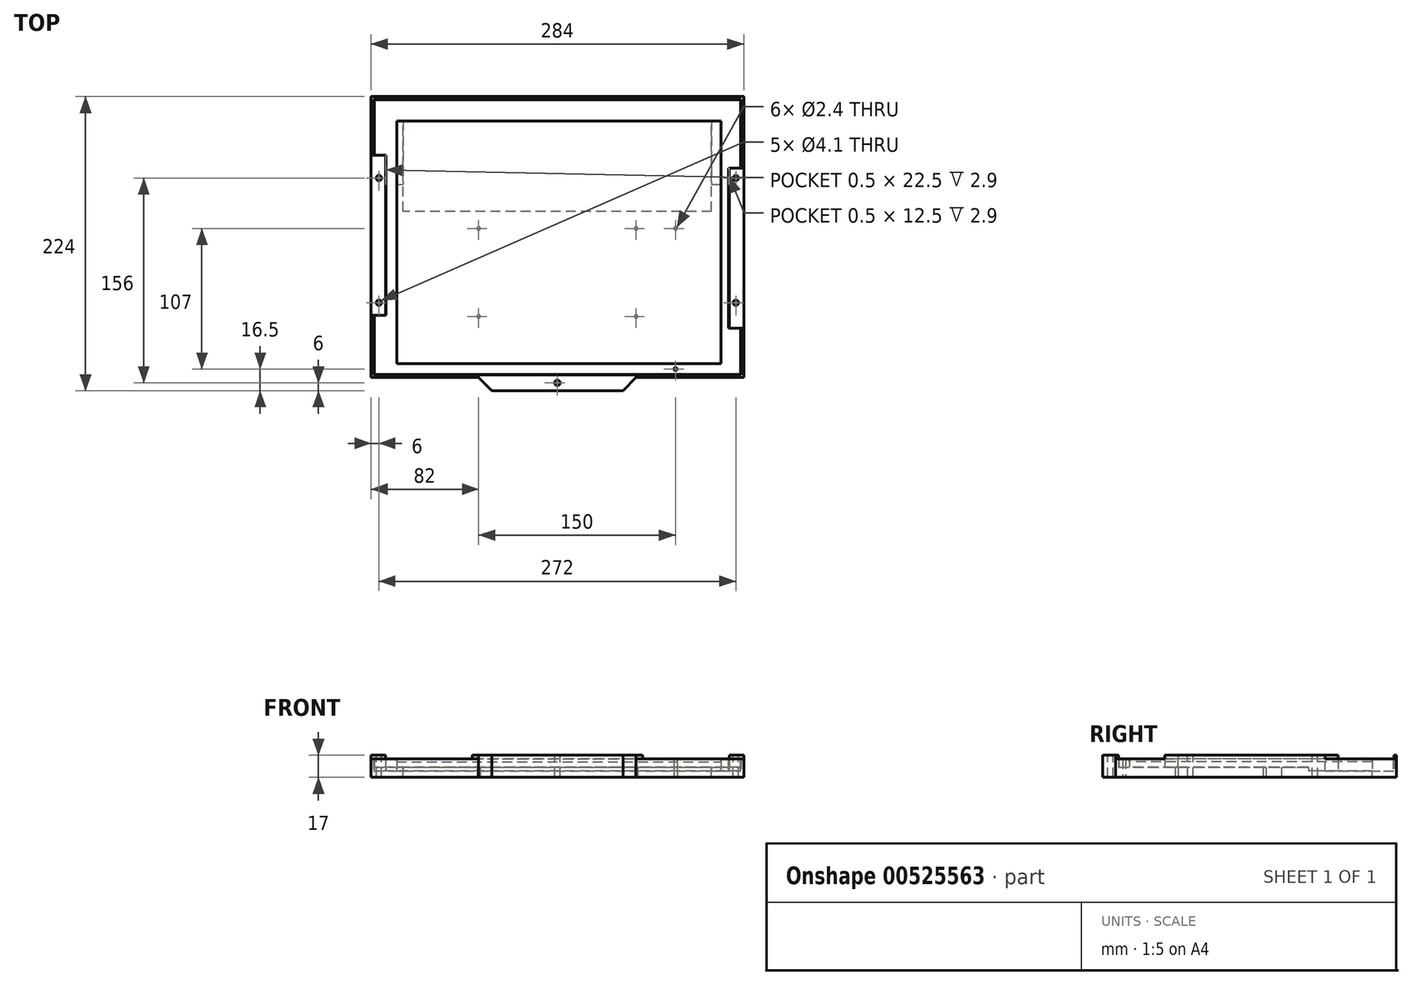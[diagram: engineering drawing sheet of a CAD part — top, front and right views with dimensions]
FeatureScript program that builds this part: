
annotation { "Feature Type Name" : "Feature", "Feature Type Description" : "" }
export const myFeature = defineFeature(function(context is Context, id is Id, definition is map)
    precondition{}
    {
        {
            var Q0;
            Q0=qCreatedBy(makeId("Top.planeOp"),FACE);
            var sketch = newSketch(context, id + "F0", { "sketchPlane" : qUnion([Q0])});
            skLineSegment(sketch, "E0.bottom", {"start": v(139.5, -104.5) * mm, "end": v(-139.5, -104.5) * mm});
            skLineSegment(sketch, "E0.top", {"start": v(139.5, 104.5) * mm, "end": v(-139.5, 104.5) * mm});
            skLineSegment(sketch, "E0.left", {"start": v(139.5, -104.5) * mm, "end": v(139.5, 104.5) * mm});
            skLineSegment(sketch, "E0.right", {"start": v(-139.5, -104.5) * mm, "end": v(-139.5, 104.5) * mm});
            skPoint(sketch, "E0.middle", {"position": v(0, 0) * mm});
            skLineSegment(sketch, "E1.bottom", {"start": v(-122.5, 88.5) * mm, "end": v(124.5, 88.5) * mm});
            skLineSegment(sketch, "E1.top", {"start": v(-122.5, -96.5) * mm, "end": v(124.5, -96.5) * mm});
            skLineSegment(sketch, "E1.left", {"start": v(-122.5, 88.5) * mm, "end": v(-122.5, -96.5) * mm});
            skLineSegment(sketch, "E1.right", {"start": v(124.5, 88.5) * mm, "end": v(124.5, -96.5) * mm});
            skSolve(sketch);
        }
        {
            var Q0;
            Q0 = qSketchRegion(id + "F0", true);
            extrude(context, id + "F1", {"entities" : qUnion([Q0]), "depth" : 9 * mm, "offsetDistance" : 25 * mm});
        }
        {
            var Q0;
            Q0=makeQuery(id+"F1.opExtrude","CAP_FACE",FACE,{"disambiguationData":[OSD([sQuery(id+"F0.wireOp",EDGE,"E0.bottom"),sQuery(id+"F0.wireOp",EDGE,"E0.top"),sQuery(id+"F0.wireOp",EDGE,"E0.left"),sQuery(id+"F0.wireOp",EDGE,"E0.right"),sQuery(id+"F0.wireOp",EDGE,"E1.bottom"),sQuery(id+"F0.wireOp",EDGE,"E1.top"),sQuery(id+"F0.wireOp",EDGE,"E1.left"),sQuery(id+"F0.wireOp",EDGE,"E1.right")])],"isStart":false});
            var sketch = newSketch(context, id + "F2", { "sketchPlane" : qUnion([Q0])});
            skLineSegment(sketch, "E2.bottom", {"start": v(-139.5, 62.5) * mm, "end": v(-130.5, 62.5) * mm});
            skLineSegment(sketch, "E2.top", {"start": v(-139.5, -59.5) * mm, "end": v(-130.5, -59.5) * mm});
            skLineSegment(sketch, "E2.left", {"start": v(-139.5, 62.5) * mm, "end": v(-139.5, -59.5) * mm});
            skLineSegment(sketch, "E2.right", {"start": v(-130.5, 62.5) * mm, "end": v(-130.5, -59.5) * mm});
            skLineSegment(sketch, "E3.bottom", {"start": v(130.5, 52.5) * mm, "end": v(139.5, 52.5) * mm});
            skLineSegment(sketch, "E3.top", {"start": v(130.5, -69.5) * mm, "end": v(139.5, -69.5) * mm});
            skLineSegment(sketch, "E3.left", {"start": v(130.5, 52.5) * mm, "end": v(130.5, -69.5) * mm});
            skLineSegment(sketch, "E3.right", {"start": v(139.5, 52.5) * mm, "end": v(139.5, -69.5) * mm});
            skSolve(sketch);
        }
        {
            var Q0;
            Q0 = qSketchRegion(id + "F2", true);
            extrude(context, id + "F3", {"entities" : qUnion([Q0]), "operationType" : NewBodyOperationType.REMOVE, "oppositeDirection" : true, "depth" : 25 * mm, "offsetDistance" : 25 * mm});
        }
        {
            var Q0;
            Q0=qCreatedBy(makeId("Top.planeOp"),FACE);
            cPlane(context, id + "F4", {"entities" : qUnion([Q0]), "cplaneType" : CPlaneType.OFFSET, "offset" : 5 * mm, "oppositeDirection" : true, "width" : 150 * mm, "height" : 150 * mm});
        }
        {
            var Q0;
            Q0=qCreatedBy(id+"F4.planeOp",FACE);
            var sketch = newSketch(context, id + "F5", { "sketchPlane" : qUnion([Q0])});
            skLineSegment(sketch, "E4.bottom", {"start": v(-142, 107) * mm, "end": v(142, 107) * mm});
            skLineSegment(sketch, "E4.top", {"start": v(-142, -107) * mm, "end": v(142, -107) * mm});
            skLineSegment(sketch, "E4.left", {"start": v(-142, 107) * mm, "end": v(-142, -107) * mm});
            skLineSegment(sketch, "E4.right", {"start": v(142, 107) * mm, "end": v(142, -107) * mm});
            skLineSegment(sketch, "E5", {"start": v(-140, 105) * mm, "end": v(140, 105) * mm});
            skLineSegment(sketch, "E6", {"start": v(140, 105) * mm, "end": v(140, 52.5) * mm});
            skLineSegment(sketch, "E7", {"start": v(140, 52.5) * mm, "end": v(131, 52.5) * mm});
            skLineSegment(sketch, "E8", {"start": v(131, 52.5) * mm, "end": v(131, -69.5) * mm});
            skLineSegment(sketch, "E9", {"start": v(131, -69.5) * mm, "end": v(140, -69.5) * mm});
            skLineSegment(sketch, "E10", {"start": v(140, -69.5) * mm, "end": v(140, -105) * mm});
            skLineSegment(sketch, "E11", {"start": v(140, -105) * mm, "end": v(-140, -105) * mm});
            skLineSegment(sketch, "E12", {"start": v(-140, -105) * mm, "end": v(-140, -59.5) * mm});
            skLineSegment(sketch, "E13", {"start": v(-140, -59.5) * mm, "end": v(-131, -59.5) * mm});
            skLineSegment(sketch, "E14", {"start": v(-131, -59.5) * mm, "end": v(-131, 62.5) * mm});
            skLineSegment(sketch, "E15", {"start": v(-131, 62.5) * mm, "end": v(-140, 62.5) * mm});
            skLineSegment(sketch, "E16", {"start": v(-140, 62.5) * mm, "end": v(-140, 105) * mm});
            skLineSegment(sketch, "E17", {"start": v(-50, -117) * mm, "end": v(50, -117) * mm});
            skLineSegment(sketch, "E18", {"start": v(50, -117) * mm, "end": v(60, -107) * mm});
            skLineSegment(sketch, "E19", {"start": v(-50, -117) * mm, "end": v(-60, -107) * mm});
            skSolve(sketch);
        }
        {
            var Q0;
            Q0 = qSketchRegion(id + "F5", true);
            extrude(context, id + "F6", {"entities" : qUnion([Q0]), "depth" : 14 * mm, "offsetDistance" : 25 * mm});
        }
        {
            var Q0;
            Q0=makeQuery(id+"F6.opExtrude","CAP_FACE",FACE,{"disambiguationData":[OSD([sQuery(id+"F5.wireOp",EDGE,"E4.bottom"),sQuery(id+"F5.wireOp",EDGE,"E4.top"),sQuery(id+"F5.wireOp",EDGE,"E4.left"),sQuery(id+"F5.wireOp",EDGE,"E4.right"),sQuery(id+"F5.wireOp",EDGE,"E5"),sQuery(id+"F5.wireOp",EDGE,"E6"),sQuery(id+"F5.wireOp",EDGE,"E7"),sQuery(id+"F5.wireOp",EDGE,"E8"),sQuery(id+"F5.wireOp",EDGE,"E9"),sQuery(id+"F5.wireOp",EDGE,"E10"),sQuery(id+"F5.wireOp",EDGE,"E11"),sQuery(id+"F5.wireOp",EDGE,"E12"),sQuery(id+"F5.wireOp",EDGE,"E13"),sQuery(id+"F5.wireOp",EDGE,"E14"),sQuery(id+"F5.wireOp",EDGE,"E15"),sQuery(id+"F5.wireOp",EDGE,"E16")])],"isStart":true});
            var sketch = newSketch(context, id + "F7", { "sketchPlane" : qUnion([Q0])});
            skLineSegment(sketch, "E20.bottom", {"start": v(140, 105) * mm, "end": v(-140, 105) * mm});
            skLineSegment(sketch, "E20.top", {"start": v(140, -105) * mm, "end": v(-140, -105) * mm});
            skLineSegment(sketch, "E20.left", {"start": v(140, 105) * mm, "end": v(140, -105) * mm});
            skLineSegment(sketch, "E20.right", {"start": v(-140, 105) * mm, "end": v(-140, -105) * mm});
            skSolve(sketch);
        }
        {
            var Q0;
            Q0 = qSketchRegion(id + "F7", true);
            extrude(context, id + "F8", {"entities" : qUnion([Q0]), "operationType" : NewBodyOperationType.ADD, "oppositeDirection" : true, "depth" : 5 * mm, "offsetDistance" : 25 * mm});
        }
        {
            var Q0;
            Q0=makeQuery(id+"F8.opExtrude","CAP_FACE",FACE,{"disambiguationData":[OSD([sQuery(id+"F7.wireOp",EDGE,"E20.bottom"),sQuery(id+"F7.wireOp",EDGE,"E20.top"),sQuery(id+"F7.wireOp",EDGE,"E20.left"),sQuery(id+"F7.wireOp",EDGE,"E20.right")])],"isStart":false});
            var sketch = newSketch(context, id + "F9", { "sketchPlane" : qUnion([Q0])});
            skPoint(sketch, "E21.oppositeSnap0", {"position": v(140, -87.25) * mm});
            skLineSegment(sketch, "E21.bottom", {"start": v(-140, -105) * mm, "end": v(140, -105) * mm});
            skLineSegment(sketch, "E21.top", {"start": v(-140, 40) * mm, "end": v(140, 40) * mm});
            skLineSegment(sketch, "E21.left", {"start": v(-140, -105) * mm, "end": v(-140, 40) * mm});
            skLineSegment(sketch, "E21.right", {"start": v(140, -105) * mm, "end": v(140, 40) * mm});
            skSolve(sketch);
        }
        {
            var Q0;
            Q0 = qSketchRegion(id + "F9", true);
            extrude(context, id + "F10", {"entities" : qUnion([Q0]), "operationType" : NewBodyOperationType.ADD, "depth" : 2.9 * mm, "offsetDistance" : 25 * mm});
        }
        {
            var Q0;
            Q0=makeQuery(id+"F10.opExtrude","CAP_FACE",FACE,{"disambiguationData":[OSD([sQuery(id+"F9.wireOp",EDGE,"E21.bottom"),sQuery(id+"F9.wireOp",EDGE,"E21.top"),sQuery(id+"F9.wireOp",EDGE,"E21.left"),sQuery(id+"F9.wireOp",EDGE,"E21.right")])],"isStart":false});
            var sketch = newSketch(context, id + "F11", { "sketchPlane" : qUnion([Q0])});
            skLineSegment(sketch, "E22.bottom", {"start": v(117.5, 19.5) * mm, "end": v(-117.5, 19.5) * mm});
            skLineSegment(sketch, "E22.top", {"start": v(117.5, 88.5) * mm, "end": v(-117.5, 88.5) * mm});
            skLineSegment(sketch, "E22.left", {"start": v(117.5, 19.5) * mm, "end": v(117.5, 88.5) * mm});
            skLineSegment(sketch, "E22.right", {"start": v(-117.5, 19.5) * mm, "end": v(-117.5, 88.5) * mm});
            skPoint(sketch, "E22.middle", {"position": v(0, 54) * mm});
            skPoint(sketch, "E23", {"position": v(0, 40) * mm});
            skSolve(sketch);
        }
        {
            var Q0;
            Q0 = qSketchRegion(id + "F11", true);
            extrude(context, id + "F12", {"entities" : qUnion([Q0]), "operationType" : NewBodyOperationType.REMOVE, "oppositeDirection" : true, "depth" : 25 * mm, "offsetDistance" : 25 * mm});
        }
        {
            var Q0;
            Q0=makeQuery(id+"F8.boolean.opBoolean","MERGE",FACE,{"derivedFrom":[makeQuery(id+"F6.opExtrude","CAP_FACE",FACE,{"disambiguationData":[OSD([sQuery(id+"F5.wireOp",EDGE,"E4.bottom"),sQuery(id+"F5.wireOp",EDGE,"E4.top"),sQuery(id+"F5.wireOp",EDGE,"E4.left"),sQuery(id+"F5.wireOp",EDGE,"E4.right"),sQuery(id+"F5.wireOp",EDGE,"E5"),sQuery(id+"F5.wireOp",EDGE,"E6"),sQuery(id+"F5.wireOp",EDGE,"E7"),sQuery(id+"F5.wireOp",EDGE,"E8"),sQuery(id+"F5.wireOp",EDGE,"E9"),sQuery(id+"F5.wireOp",EDGE,"E10"),sQuery(id+"F5.wireOp",EDGE,"E11"),sQuery(id+"F5.wireOp",EDGE,"E12"),sQuery(id+"F5.wireOp",EDGE,"E13"),sQuery(id+"F5.wireOp",EDGE,"E14"),sQuery(id+"F5.wireOp",EDGE,"E15"),sQuery(id+"F5.wireOp",EDGE,"E16")])],"isStart":true}),makeQuery(id+"F8.opExtrude","CAP_FACE",FACE,{"disambiguationData":[OSD([sQuery(id+"F7.wireOp",EDGE,"E20.bottom"),sQuery(id+"F7.wireOp",EDGE,"E20.top"),sQuery(id+"F7.wireOp",EDGE,"E20.left"),sQuery(id+"F7.wireOp",EDGE,"E20.right")])],"isStart":true})]});
            var sketch = newSketch(context, id + "F13", { "sketchPlane" : qUnion([Q0])});
            skCircle(sketch, "E24", {"center": v(50, 62.5) * mm, "radius": 1.2 * mm, "construction": true});
            skCircle(sketch, "E25", {"center": v(-50, 62.5) * mm, "radius": 1.2 * mm, "construction": true});
            skCircle(sketch, "E26", {"center": v(3.5, 17.5) * mm, "radius": 1.2 * mm, "construction": true});
            skLineSegment(sketch, "E27.bottom", {"start": v(-53.5, 64.5) * mm, "end": v(53.5, 64.5) * mm, "construction": true});
            skLineSegment(sketch, "E27.top", {"start": v(-53.5, -10.5) * mm, "end": v(53.5, -10.5) * mm, "construction": true});
            skLineSegment(sketch, "E27.left", {"start": v(-53.5, 64.5) * mm, "end": v(-53.5, -10.5) * mm, "construction": true});
            skLineSegment(sketch, "E27.right", {"start": v(53.5, 64.5) * mm, "end": v(53.5, -10.5) * mm, "construction": true});
            skPoint(sketch, "E27.middle", {"position": v(0, 27) * mm});
            skCircle(sketch, "E28", {"center": v(90, -6.5) * mm, "radius": 1.2 * mm});
            skCircle(sketch, "E29", {"center": v(90, 100.5) * mm, "radius": 1.2 * mm});
            skCircle(sketch, "E30", {"center": v(60, 60.5) * mm, "radius": 1.2 * mm});
            skCircle(sketch, "E31", {"center": v(60, -6.5) * mm, "radius": 1.2 * mm});
            skCircle(sketch, "E32.MirrorC", {"center": v(-60, 60.5) * mm, "radius": 1.2 * mm});
            skCircle(sketch, "E33.MirrorC", {"center": v(-60, -6.5) * mm, "radius": 1.2 * mm});
            skSolve(sketch);
        }
        {
            var Q0;
            Q0 = qSketchRegion(id + "F13", true);
            extrude(context, id + "F14", {"entities" : qUnion([Q0]), "operationType" : NewBodyOperationType.REMOVE, "oppositeDirection" : true, "depth" : 25 * mm, "offsetDistance" : 25 * mm});
        }
        {
            var Q0;
            Q0=makeQuery(id+"F6.opExtrude","CAP_FACE",FACE,{"disambiguationData":[OSD([sQuery(id+"F5.wireOp",EDGE,"E4.bottom"),sQuery(id+"F5.wireOp",EDGE,"E4.top"),sQuery(id+"F5.wireOp",EDGE,"E4.left"),sQuery(id+"F5.wireOp",EDGE,"E4.right"),sQuery(id+"F5.wireOp",EDGE,"E5"),sQuery(id+"F5.wireOp",EDGE,"E6"),sQuery(id+"F5.wireOp",EDGE,"E7"),sQuery(id+"F5.wireOp",EDGE,"E8"),sQuery(id+"F5.wireOp",EDGE,"E9"),sQuery(id+"F5.wireOp",EDGE,"E10"),sQuery(id+"F5.wireOp",EDGE,"E11"),sQuery(id+"F5.wireOp",EDGE,"E12"),sQuery(id+"F5.wireOp",EDGE,"E13"),sQuery(id+"F5.wireOp",EDGE,"E14"),sQuery(id+"F5.wireOp",EDGE,"E15"),sQuery(id+"F5.wireOp",EDGE,"E16")])],"isStart":false});
            var sketch = newSketch(context, id + "F15", { "sketchPlane" : qUnion([Q0])});
            skLineSegment(sketch, "E34.bottom", {"start": v(-131, 62.5) * mm, "end": v(-142, 62.5) * mm});
            skLineSegment(sketch, "E34.top", {"start": v(-131, -59.5) * mm, "end": v(-142, -59.5) * mm});
            skLineSegment(sketch, "E34.left", {"start": v(-131, 62.5) * mm, "end": v(-131, -59.5) * mm});
            skLineSegment(sketch, "E34.right", {"start": v(-142, 62.5) * mm, "end": v(-142, -59.5) * mm});
            skLineSegment(sketch, "E35.bottom", {"start": v(131, 52.5) * mm, "end": v(142, 52.5) * mm});
            skLineSegment(sketch, "E35.top", {"start": v(131, -69.5) * mm, "end": v(142, -69.5) * mm});
            skLineSegment(sketch, "E35.left", {"start": v(131, 52.5) * mm, "end": v(131, -69.5) * mm});
            skLineSegment(sketch, "E35.right", {"start": v(142, 52.5) * mm, "end": v(142, -69.5) * mm});
            skLineSegment(sketch, "E36.bottom", {"start": v(-142, -107) * mm, "end": v(-112, -107) * mm, "construction": true});
            skLineSegment(sketch, "E36.top", {"start": v(-142, -105) * mm, "end": v(-112, -105) * mm, "construction": true});
            skLineSegment(sketch, "E36.left", {"start": v(-142, -107) * mm, "end": v(-142, -105) * mm, "construction": true});
            skLineSegment(sketch, "E36.right", {"start": v(-112, -107) * mm, "end": v(-112, -105) * mm, "construction": true});
            skLineSegment(sketch, "E37.bottom", {"start": v(142, -107) * mm, "end": v(112, -107) * mm, "construction": true});
            skLineSegment(sketch, "E37.top", {"start": v(142, -105) * mm, "end": v(112, -105) * mm, "construction": true});
            skLineSegment(sketch, "E37.left", {"start": v(142, -107) * mm, "end": v(142, -105) * mm, "construction": true});
            skLineSegment(sketch, "E37.right", {"start": v(112, -107) * mm, "end": v(112, -105) * mm, "construction": true});
            skLineSegment(sketch, "E38.bottom", {"start": v(-65, 107) * mm, "end": v(65, 107) * mm});
            skLineSegment(sketch, "E38.top", {"start": v(-65, 105) * mm, "end": v(65, 105) * mm});
            skLineSegment(sketch, "E38.left", {"start": v(-65, 107) * mm, "end": v(-65, 105) * mm});
            skLineSegment(sketch, "E38.right", {"start": v(65, 107) * mm, "end": v(65, 105) * mm});
            skLineSegment(sketch, "E39", {"start": v(-50, -117) * mm, "end": v(50, -117) * mm});
            skLineSegment(sketch, "E40", {"start": v(50, -117) * mm, "end": v(60, -107) * mm});
            skLineSegment(sketch, "E41", {"start": v(60, -107) * mm, "end": v(60, -105) * mm});
            skLineSegment(sketch, "E42", {"start": v(60, -105) * mm, "end": v(-60, -105) * mm});
            skLineSegment(sketch, "E43", {"start": v(-60, -105) * mm, "end": v(-60, -107) * mm});
            skLineSegment(sketch, "E44", {"start": v(-60, -107) * mm, "end": v(-50, -117) * mm});
            skSolve(sketch);
        }
        {
            var Q0;
            Q0 = qSketchRegion(id + "F15", true);
            extrude(context, id + "F16", {"entities" : qUnion([Q0]), "operationType" : NewBodyOperationType.ADD, "depth" : 3 * mm, "offsetDistance" : 25 * mm});
        }
        {
            var Q0;
            Q0=makeQuery(id+"F16.opExtrude","CAP_FACE",FACE,{"disambiguationData":[OSD([sQuery(id+"F15.wireOp",EDGE,"E34.bottom"),sQuery(id+"F15.wireOp",EDGE,"E34.top"),sQuery(id+"F15.wireOp",EDGE,"E34.left"),sQuery(id+"F15.wireOp",EDGE,"E34.right")])],"isStart":false});
            var sketch = newSketch(context, id + "F17", { "sketchPlane" : qUnion([Q0])});
            skCircle(sketch, "E45", {"center": v(-136, 45) * mm, "radius": 2.05 * mm});
            skCircle(sketch, "E46", {"center": v(-136, 0) * mm, "radius": 2.05 * mm, "construction": true});
            skCircle(sketch, "E47", {"center": v(-136, -50) * mm, "radius": 2.05 * mm});
            skCircle(sketch, "E48.MirrorC", {"center": v(136, 0) * mm, "radius": 2.05 * mm, "construction": true});
            skCircle(sketch, "E49.MirrorC", {"center": v(136, -50) * mm, "radius": 2.05 * mm});
            skCircle(sketch, "E50.MirrorC", {"center": v(136, 45) * mm, "radius": 2.05 * mm});
            skCircle(sketch, "E51", {"center": v(0, -111) * mm, "radius": 2.05 * mm});
            skSolve(sketch);
        }
        {
            var Q0;
            Q0 = qSketchRegion(id + "F17", true);
            extrude(context, id + "F18", {"entities" : qUnion([Q0]), "operationType" : NewBodyOperationType.REMOVE, "oppositeDirection" : true, "depth" : 25 * mm, "offsetDistance" : 25 * mm});
        }
        {
            var Q0;
            Q0=makeQuery(id+"F1.opExtrude","CAP_FACE",FACE,{"disambiguationData":[OSD([sQuery(id+"F0.wireOp",EDGE,"E0.bottom"),sQuery(id+"F0.wireOp",EDGE,"E0.top"),sQuery(id+"F0.wireOp",EDGE,"E0.left"),sQuery(id+"F0.wireOp",EDGE,"E0.right"),sQuery(id+"F0.wireOp",EDGE,"E1.bottom"),sQuery(id+"F0.wireOp",EDGE,"E1.top"),sQuery(id+"F0.wireOp",EDGE,"E1.left"),sQuery(id+"F0.wireOp",EDGE,"E1.right")])],"isStart":false});
            var sketch = newSketch(context, id + "F19", { "sketchPlane" : qUnion([Q0])});
            skLineSegment(sketch, "E52.bottom", {"start": v(-122.5, 88.5) * mm, "end": v(124.5, 88.5) * mm});
            skLineSegment(sketch, "E52.top", {"start": v(-122.5, -96.5) * mm, "end": v(124.5, -96.5) * mm});
            skLineSegment(sketch, "E52.left", {"start": v(-122.5, 88.5) * mm, "end": v(-122.5, -96.5) * mm});
            skLineSegment(sketch, "E52.right", {"start": v(124.5, 88.5) * mm, "end": v(124.5, -96.5) * mm});
            skSolve(sketch);
        }
        {
            var Q0;
            Q0 = qSketchRegion(id + "F19", true);
            extrude(context, id + "F20", {"entities" : qUnion([Q0]), "oppositeDirection" : true, "depth" : 2 * mm, "offsetDistance" : 25 * mm});
        }
    });
